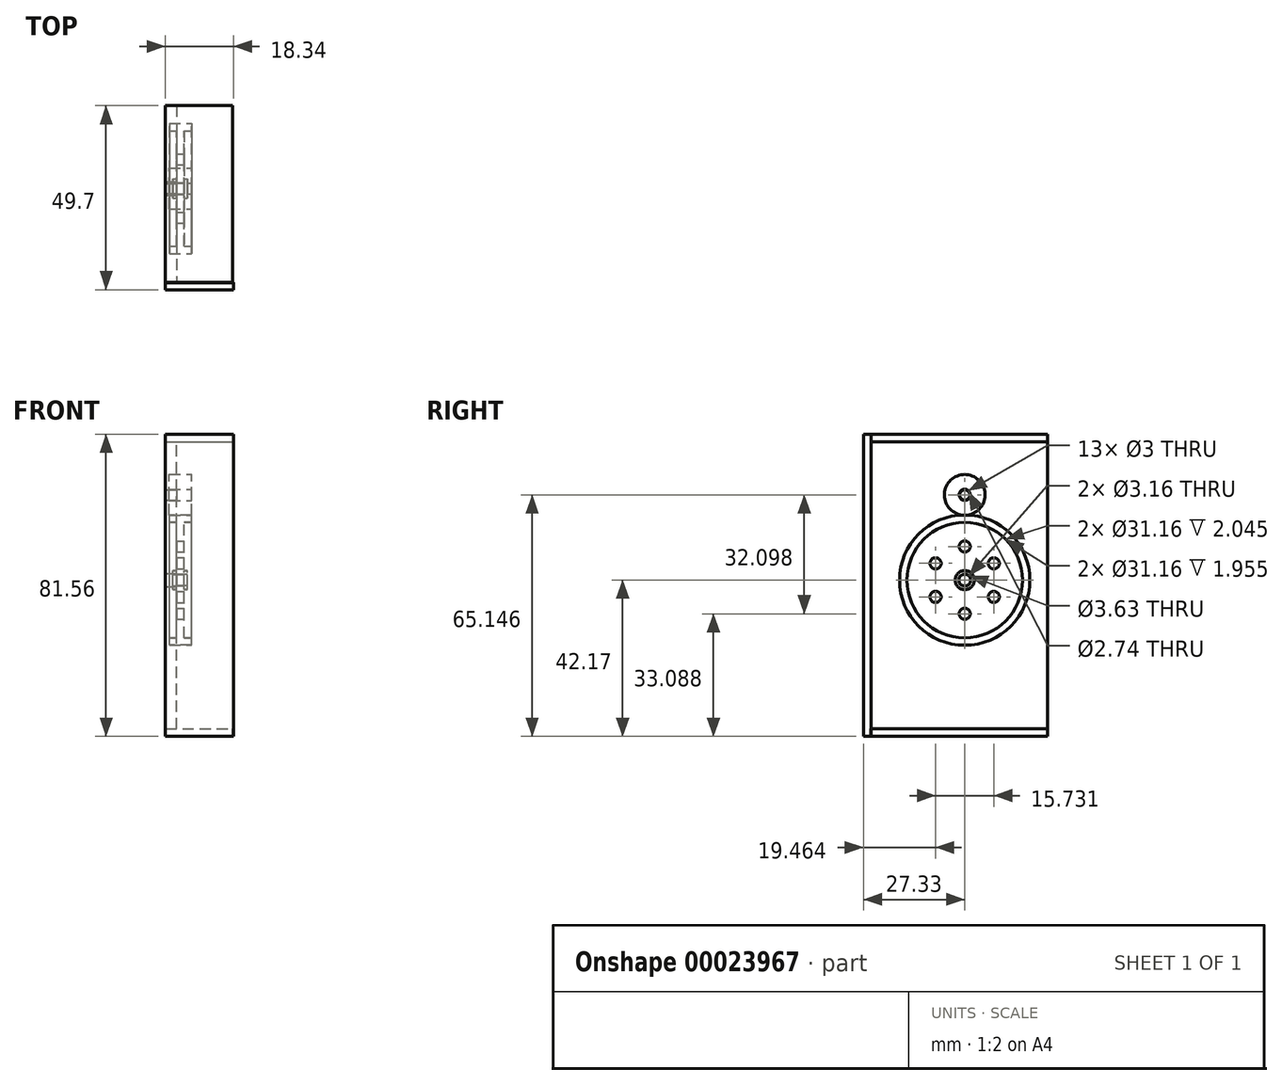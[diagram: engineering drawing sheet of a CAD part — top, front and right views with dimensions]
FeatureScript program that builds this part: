
annotation { "Feature Type Name" : "Feature", "Feature Type Description" : "" }
export const myFeature = defineFeature(function(context is Context, id is Id, definition is map)
    precondition{}
    {
        {
            var Q0;
            Q0=qCreatedBy(makeId("Front.planeOp"),FACE);
            var sketch = newSketch(context, id + "F0", { "sketchPlane" : qUnion([Q0])});
            skLineSegment(sketch, "E0", {"start": v(0, 0) * mm, "end": v(-24.04, 0) * mm, "construction": true});
            skLineSegment(sketch, "E1", {"start": v(0, 0) * mm, "end": v(17.15, 0) * mm, "construction": true});
            skLineSegment(sketch, "E2", {"start": v(-24.13, 1.5) * mm, "end": v(17.07, 1.5) * mm});
            skLineSegment(sketch, "E3.top", {"start": v(12.35, 2.58) * mm, "end": v(10.35, 2.58) * mm});
            skLineSegment(sketch, "E3.left", {"start": v(12.35, 15.58) * mm, "end": v(12.35, 2.58) * mm});
            skLineSegment(sketch, "E3.right", {"start": v(10.35, 15.58) * mm, "end": v(10.35, 2.58) * mm});
            skLineSegment(sketch, "E4.bottom", {"start": v(9.32, 2.58) * mm, "end": v(13.32, 2.58) * mm});
            skLineSegment(sketch, "E4.top", {"start": v(9.32, 1.58) * mm, "end": v(13.32, 1.58) * mm});
            skLineSegment(sketch, "E4.left", {"start": v(9.32, 2.58) * mm, "end": v(9.32, 1.58) * mm});
            skLineSegment(sketch, "E4.right", {"start": v(13.32, 2.58) * mm, "end": v(13.32, 1.58) * mm});
            skLineSegment(sketch, "E5", {"start": v(10.35, 15.58) * mm, "end": v(12.35, 15.58) * mm});
            skLineSegment(sketch, "E6.bottom", {"start": v(8.4, 15.58) * mm, "end": v(14.4, 15.58) * mm});
            skLineSegment(sketch, "E6.top", {"start": v(8.4, 17.58) * mm, "end": v(14.4, 17.58) * mm});
            skLineSegment(sketch, "E6.left", {"start": v(8.4, 15.58) * mm, "end": v(8.4, 17.58) * mm});
            skLineSegment(sketch, "E6.right", {"start": v(14.4, 15.58) * mm, "end": v(14.4, 17.58) * mm});
            skLineSegment(sketch, "E7.top", {"start": v(-14.98, 1.5) * mm, "end": v(-12.94, 1.5) * mm});
            skLineSegment(sketch, "E8", {"start": v(-24.16, 1) * mm, "end": v(17.07, 1) * mm});
            skLineSegment(sketch, "E9.top", {"start": v(8.4, 17.44) * mm, "end": v(14.4, 17.44) * mm});
            skSolve(sketch);
        }
        {
            var Q0;
            Q0 = qSketchRegion(id + "F0", true);
            var Q1;
            Q1=sQuery(id+"F0.wireOp",EDGE,"E1");
            revolve(context, id + "F1", {"entities" : qUnion([Q0]), "axis" : qUnion([Q1]), "revolveType" : RevolveType.FULL});
        }
        {
            var Q0;
            Q0 = qSketchRegion(id + "F0", true);
            var Q1;
            Q1=sQuery(id+"F0.wireOp",EDGE,"E0");
            revolve(context, id + "F2", {"entities" : qUnion([Q0]), "axis" : qUnion([Q1]), "revolveType" : RevolveType.FULL});
        }
        {
            var Q0;
            Q0=makeQuery(id+"F1.opRevolve","SWEPT_FACE",FACE,{"disambiguationData":[OSD([sQuery(id+"F0.wireOp",EDGE,"E3.left")])]});
            var sketch = newSketch(context, id + "F3", { "sketchPlane" : qUnion([Q0])});
            skLineSegment(sketch, "E10", {"start": v(0, 2.58) * mm, "end": v(0, 9.08) * mm, "construction": true});
            skCircle(sketch, "E11", {"center": v(0, 9.08) * mm, "radius": 1.5 * mm});
            skCircle(sketch, "E12.1.0", {"center": v(-7.87, 4.54) * mm, "radius": 1.5 * mm});
            skCircle(sketch, "E12.2.0", {"center": v(-7.87, -4.54) * mm, "radius": 1.5 * mm});
            skCircle(sketch, "E12.3.0", {"center": v(0, -9.08) * mm, "radius": 1.5 * mm});
            skCircle(sketch, "E12.4.0", {"center": v(7.87, -4.54) * mm, "radius": 1.5 * mm});
            skCircle(sketch, "E12.5.0", {"center": v(7.87, 4.54) * mm, "radius": 1.5 * mm});
            skPoint(sketch, "E12.center", {"position": v(0, 0) * mm});
            skSolve(sketch);
        }
        {
            var Q0;
            Q0=makeQuery(id+"F3.imprint","IMPRINT",FACE,{"disambiguationData":[TD([[makeQuery(id+"F3.imprint","IMPRINT",EDGE,{"derivedFrom":sQuery(id+"F3.wireOp",EDGE,"E12.1.0")}),1.0]])]});
            var Q1;
            Q1=makeQuery(id+"F3.imprint","IMPRINT",FACE,{"disambiguationData":[TD([[makeQuery(id+"F3.imprint","IMPRINT",EDGE,{"derivedFrom":sQuery(id+"F3.wireOp",EDGE,"E12.2.0")}),1.0]])]});
            var Q2;
            Q2=makeQuery(id+"F3.imprint","IMPRINT",FACE,{"disambiguationData":[TD([[makeQuery(id+"F3.imprint","IMPRINT",EDGE,{"derivedFrom":sQuery(id+"F3.wireOp",EDGE,"E12.3.0")}),1.0]])]});
            var Q3;
            Q3=makeQuery(id+"F3.imprint","IMPRINT",FACE,{"disambiguationData":[TD([[makeQuery(id+"F3.imprint","IMPRINT",EDGE,{"derivedFrom":sQuery(id+"F3.wireOp",EDGE,"E12.4.0")}),1.0]])]});
            var Q4;
            Q4=makeQuery(id+"F3.imprint","IMPRINT",FACE,{"disambiguationData":[TD([[makeQuery(id+"F3.imprint","IMPRINT",EDGE,{"derivedFrom":sQuery(id+"F3.wireOp",EDGE,"E12.5.0")}),1.0]])]});
            var Q5;
            Q5=makeQuery(id+"F3.imprint","IMPRINT",FACE,{"disambiguationData":[TD([[makeQuery(id+"F3.imprint","IMPRINT",EDGE,{"derivedFrom":sQuery(id+"F3.wireOp",EDGE,"E11")}),1.0]])]});
            extrude(context, id + "F4", {"entities" : qUnion([Q0, Q1, Q2, Q3, Q4, Q5]), "operationType" : NewBodyOperationType.REMOVE, "endBound" : BoundingType.THROUGH_ALL, "oppositeDirection" : true, "depth" : 25.4 * mm});
        }
        {
            var Q0;
            Q0=qCreatedBy(makeId("Front.planeOp"),FACE);
            var sketch = newSketch(context, id + "F5", { "sketchPlane" : qUnion([Q0])});
            skLineSegment(sketch, "E13.bottom", {"start": v(8.36, 21.52) * mm, "end": v(14.36, 21.52) * mm});
            skLineSegment(sketch, "E13.right", {"start": v(14.36, 21.52) * mm, "end": v(14.36, 17.52) * mm});
            skLineSegment(sketch, "E13.top", {"start": v(8.36, 17.52) * mm, "end": v(14.36, 17.52) * mm});
            skLineSegment(sketch, "E13.left", {"start": v(8.36, 21.52) * mm, "end": v(8.36, 17.52) * mm});
            skLineSegment(sketch, "E14", {"start": v(27.36, 23.02) * mm, "end": v(-4.56, 23.02) * mm, "construction": true});
            skSolve(sketch);
        }
        {
            var Q0;
            Q0=makeQuery(id+"F5.imprint","IMPRINT",FACE,{"disambiguationData":[TD([[makeQuery(id+"F5.imprint","IMPRINT",EDGE,{"derivedFrom":sQuery(id+"F5.wireOp",EDGE,"E13.bottom")}),-1.0]])]});
            var Q1;
            Q1=sQuery(id+"F5.wireOp",EDGE,"E14");
            revolve(context, id + "F6", {"entities" : qUnion([Q0]), "axis" : qUnion([Q1]), "revolveType" : RevolveType.FULL});
        }
        {
            var Q0;
            Q0=makeQuery(id+"F1.opRevolve","SWEPT_FACE",FACE,{"disambiguationData":[OSD([sQuery(id+"F0.wireOp",EDGE,"E3.right")])]});
            var sketch = newSketch(context, id + "F7", { "sketchPlane" : qUnion([Q0])});
            skCircle(sketch, "E15", {"center": v(0, 0) * mm, "radius": 1.82 * mm});
            skCircle(sketch, "E16", {"center": v(0, 22.98) * mm, "radius": 1.37 * mm});
            skLineSegment(sketch, "E17.bottom", {"start": v(-22.37, -40.17) * mm, "end": v(25.33, -40.17) * mm});
            skLineSegment(sketch, "E17.top", {"start": v(-22.37, 37.39) * mm, "end": v(25.33, 37.39) * mm});
            skLineSegment(sketch, "E17.left", {"start": v(-22.37, -40.17) * mm, "end": v(-22.37, 37.39) * mm});
            skLineSegment(sketch, "E17.right", {"start": v(25.33, -40.17) * mm, "end": v(25.33, 37.39) * mm});
            skSolve(sketch);
        }
        {
            var Q0;
            Q0 = qSketchRegion(id + "F7", true);
            extrude(context, id + "F8", {"entities" : qUnion([Q0]), "depth" : 3 * mm});
        }
        {
            var Q0;
            Q0=makeQuery(id+"F8.opExtrude","SWEPT_FACE",FACE,{"disambiguationData":[OSD([sQuery(id+"F7.wireOp",EDGE,"E17.top")])]});
            var sketch = newSketch(context, id + "F9", { "sketchPlane" : qUnion([Q0])});
            skLineSegment(sketch, "E18.bottom", {"start": v(7.35, 22.37) * mm, "end": v(25.4, 22.37) * mm});
            skLineSegment(sketch, "E18.top", {"start": v(7.35, -25.47) * mm, "end": v(25.4, -25.47) * mm});
            skLineSegment(sketch, "E18.left", {"start": v(7.35, 22.37) * mm, "end": v(7.35, -25.47) * mm});
            skLineSegment(sketch, "E18.right", {"start": v(25.4, 22.37) * mm, "end": v(25.4, -25.47) * mm});
            skSolve(sketch);
        }
        {
            var Q0;
            Q0 = qSketchRegion(id + "F9", true);
            extrude(context, id + "F10", {"entities" : qUnion([Q0]), "operationType" : NewBodyOperationType.ADD, "depth" : 2 * mm});
        }
        {
            var Q0;
            Q0=makeQuery(id+"F8.opExtrude","SWEPT_FACE",FACE,{"disambiguationData":[OSD([sQuery(id+"F7.wireOp",EDGE,"E17.bottom")])]});
            var sketch = newSketch(context, id + "F11", { "sketchPlane" : qUnion([Q0])});
            skLineSegment(sketch, "E19.bottom", {"start": v(7.35, -22.37) * mm, "end": v(25.52, -22.37) * mm});
            skLineSegment(sketch, "E19.top", {"start": v(7.35, 25.47) * mm, "end": v(25.52, 25.47) * mm});
            skLineSegment(sketch, "E19.left", {"start": v(7.35, -22.37) * mm, "end": v(7.35, 25.47) * mm});
            skLineSegment(sketch, "E19.right", {"start": v(25.52, -22.37) * mm, "end": v(25.52, 25.47) * mm});
            skSolve(sketch);
        }
        {
            var Q0;
            Q0 = qSketchRegion(id + "F11", true);
            extrude(context, id + "F12", {"entities" : qUnion([Q0]), "depth" : 2 * mm});
        }
        {
            var Q0;
            Q0=makeQuery(id+"F8.opExtrude","SWEPT_FACE",FACE,{"disambiguationData":[OSD([sQuery(id+"F7.wireOp",EDGE,"E17.right")])]});
            var sketch = newSketch(context, id + "F13", { "sketchPlane" : qUnion([Q0])});
            skLineSegment(sketch, "E20.bottom", {"start": v(7.35, -42.46) * mm, "end": v(7.35, -42.46) * mm});
            skLineSegment(sketch, "E20.top", {"start": v(7.35, 39.35) * mm, "end": v(7.35, 39.35) * mm});
            skLineSegment(sketch, "E20.left", {"start": v(7.35, -42.46) * mm, "end": v(7.35, 39.35) * mm});
            skLineSegment(sketch, "E21.bottom", {"start": v(25.7, -42.17) * mm, "end": v(7.35, -42.17) * mm});
            skLineSegment(sketch, "E21.top", {"start": v(25.7, 39.39) * mm, "end": v(7.35, 39.39) * mm});
            skLineSegment(sketch, "E21.left", {"start": v(25.7, -42.17) * mm, "end": v(25.7, 39.39) * mm});
            skLineSegment(sketch, "E21.right", {"start": v(7.35, -42.17) * mm, "end": v(7.35, 39.39) * mm});
            skSolve(sketch);
        }
        {
            var Q0;
            Q0 = qSketchRegion(id + "F13", true);
            extrude(context, id + "F14", {"entities" : qUnion([Q0]), "depth" : 2 * mm});
        }
    });
